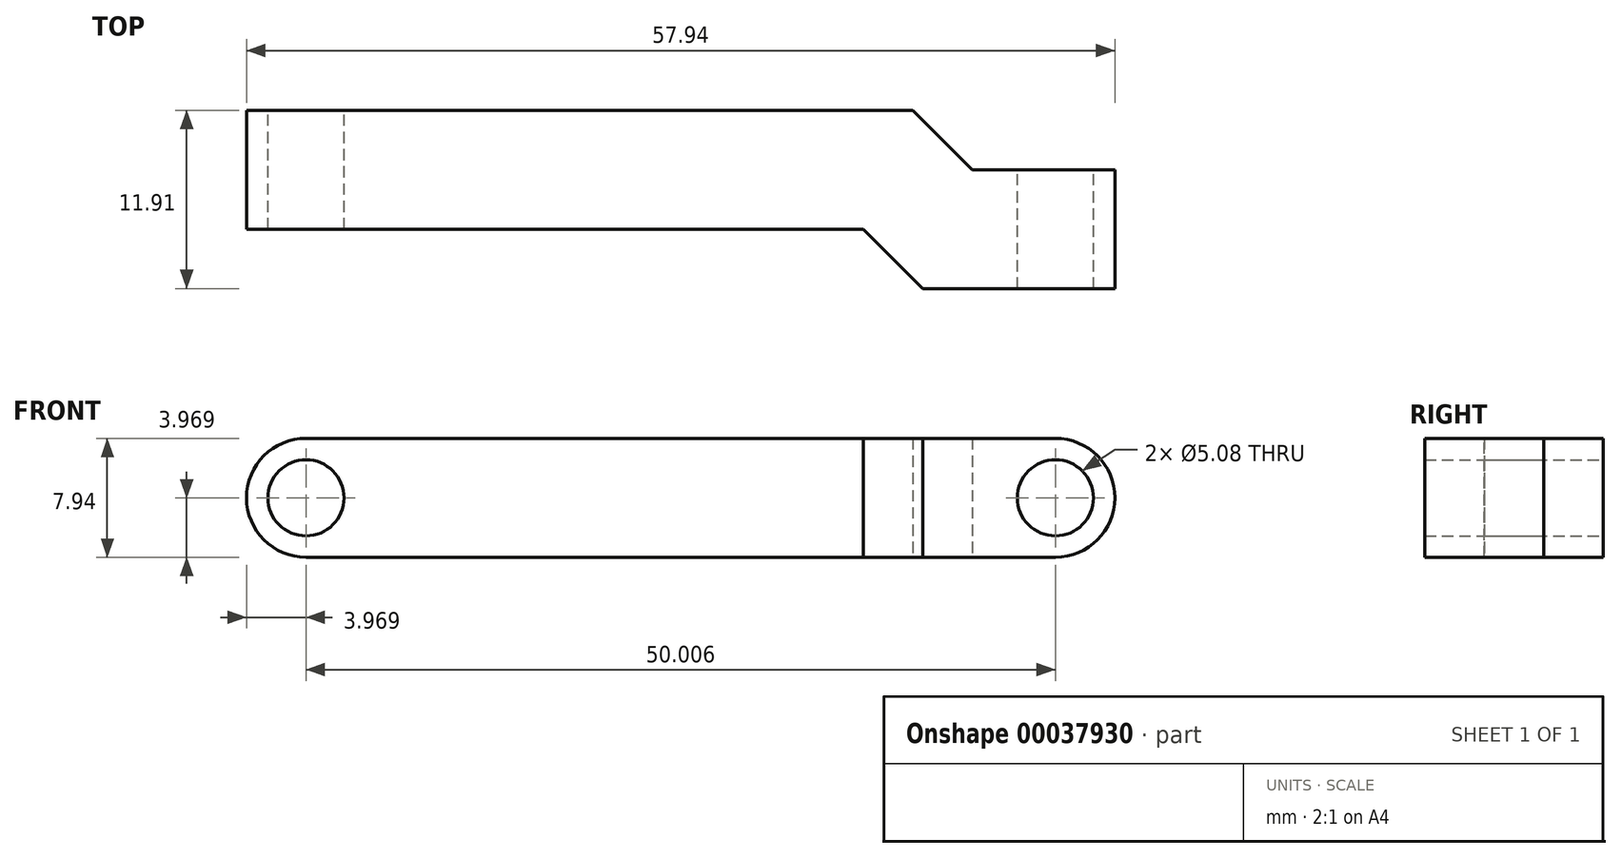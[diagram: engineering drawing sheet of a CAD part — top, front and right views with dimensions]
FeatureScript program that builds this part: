
annotation { "Feature Type Name" : "Feature", "Feature Type Description" : "" }
export const myFeature = defineFeature(function(context is Context, id is Id, definition is map)
    precondition{}
    {
        {
            var Q0;
            Q0=qCreatedBy(makeId("Top.planeOp"),FACE);
            var sketch = newSketch(context, id + "F0", { "sketchPlane" : qUnion([Q0])});
            skLineSegment(sketch, "E0.bottom", {"start": v(0, 0) * mm, "end": v(44.45, 0) * mm});
            skLineSegment(sketch, "E0.top", {"start": v(0, -7.94) * mm, "end": v(41.16, -7.94) * mm});
            skLineSegment(sketch, "E0.left", {"start": v(0, 0) * mm, "end": v(0, -7.94) * mm});
            skLineSegment(sketch, "E1", {"start": v(41.16, -7.94) * mm, "end": v(45.13, -11.9) * mm});
            skLineSegment(sketch, "E2", {"start": v(44.45, 0) * mm, "end": v(48.42, -3.97) * mm});
            skLineSegment(sketch, "E3", {"start": v(48.42, -3.97) * mm, "end": v(57.94, -3.97) * mm});
            skLineSegment(sketch, "E4", {"start": v(57.94, -3.97) * mm, "end": v(57.94, -11.9) * mm});
            skLineSegment(sketch, "E5", {"start": v(44.45, 0) * mm, "end": v(57.94, 0) * mm, "construction": true});
            skLineSegment(sketch, "E6", {"start": v(57.94, 0) * mm, "end": v(57.94, -3.97) * mm, "construction": true});
            skLineSegment(sketch, "E7", {"start": v(46.43, -1.98) * mm, "end": v(40.82, -7.6) * mm, "construction": true});
            skLineSegment(sketch, "E8", {"start": v(45.13, -11.9) * mm, "end": v(57.94, -11.9) * mm});
            skLineSegment(sketch, "E9", {"start": v(41.16, -7.94) * mm, "end": v(40.82, -7.6) * mm, "construction": true});
            skSolve(sketch);
        }
        {
            var Q0;
            Q0=qSketchRegion(id+"F0",true);
            extrude(context, id + "F1", {"entities" : qUnion([Q0]), "depth" : 7.94 * mm});
        }
        {
            var Q0;
            Q0=makeQuery(id+"F1.opExtrude","CAP_EDGE",EDGE,{"disambiguationData":[OSD([sQuery(id+"F0.wireOp",EDGE,"E0.left")])],"isStart":true});
            var Q1;
            Q1=makeQuery(id+"F1.opExtrude","CAP_EDGE",EDGE,{"disambiguationData":[OSD([sQuery(id+"F0.wireOp",EDGE,"E0.left")])],"isStart":false});
            var Q2;
            Q2=makeQuery(id+"F1.opExtrude","CAP_EDGE",EDGE,{"disambiguationData":[OSD([sQuery(id+"F0.wireOp",EDGE,"E4")])],"isStart":true});
            var Q3;
            Q3=makeQuery(id+"F1.opExtrude","CAP_EDGE",EDGE,{"disambiguationData":[OSD([sQuery(id+"F0.wireOp",EDGE,"E4")])],"isStart":false});
            fillet(context, id + "F2", {"entities" : qUnion([Q0, Q1, Q2, Q3]), "radius" : 3.97 * mm, "tangentPropagation" : true, "allowEdgeOverflow" : false});
        }
        {
            var Q0;
            Q0=makeQuery(id+"F1.opExtrude","SWEPT_FACE",FACE,{"disambiguationData":[OSD([sQuery(id+"F0.wireOp",EDGE,"E0.bottom")])]});
            var sketch = newSketch(context, id + "F3", { "sketchPlane" : qUnion([Q0])});
            skCircle(sketch, "E10", {"center": v(-3.97, 3.97) * mm, "radius": 2.54 * mm});
            skCircle(sketch, "E11", {"center": v(-53.98, 3.97) * mm, "radius": 2.54 * mm});
            skSolve(sketch);
        }
        {
            var Q0;
            Q0=qSketchRegion(id+"F3",true);
            var Q1;
            Q1=makeQuery(id+"F1.opExtrude","SWEPT_FACE",FACE,{"disambiguationData":[OSD([sQuery(id+"F0.wireOp",EDGE,"E8")])]});
            extrude(context, id + "F4", {"entities" : qUnion([Q0]), "operationType" : NewBodyOperationType.REMOVE, "endBound" : BoundingType.UP_TO_SURFACE, "oppositeDirection" : true, "endBoundEntityFace" : qUnion([Q1]), "depth" : 25.4 * mm});
        }
    });
